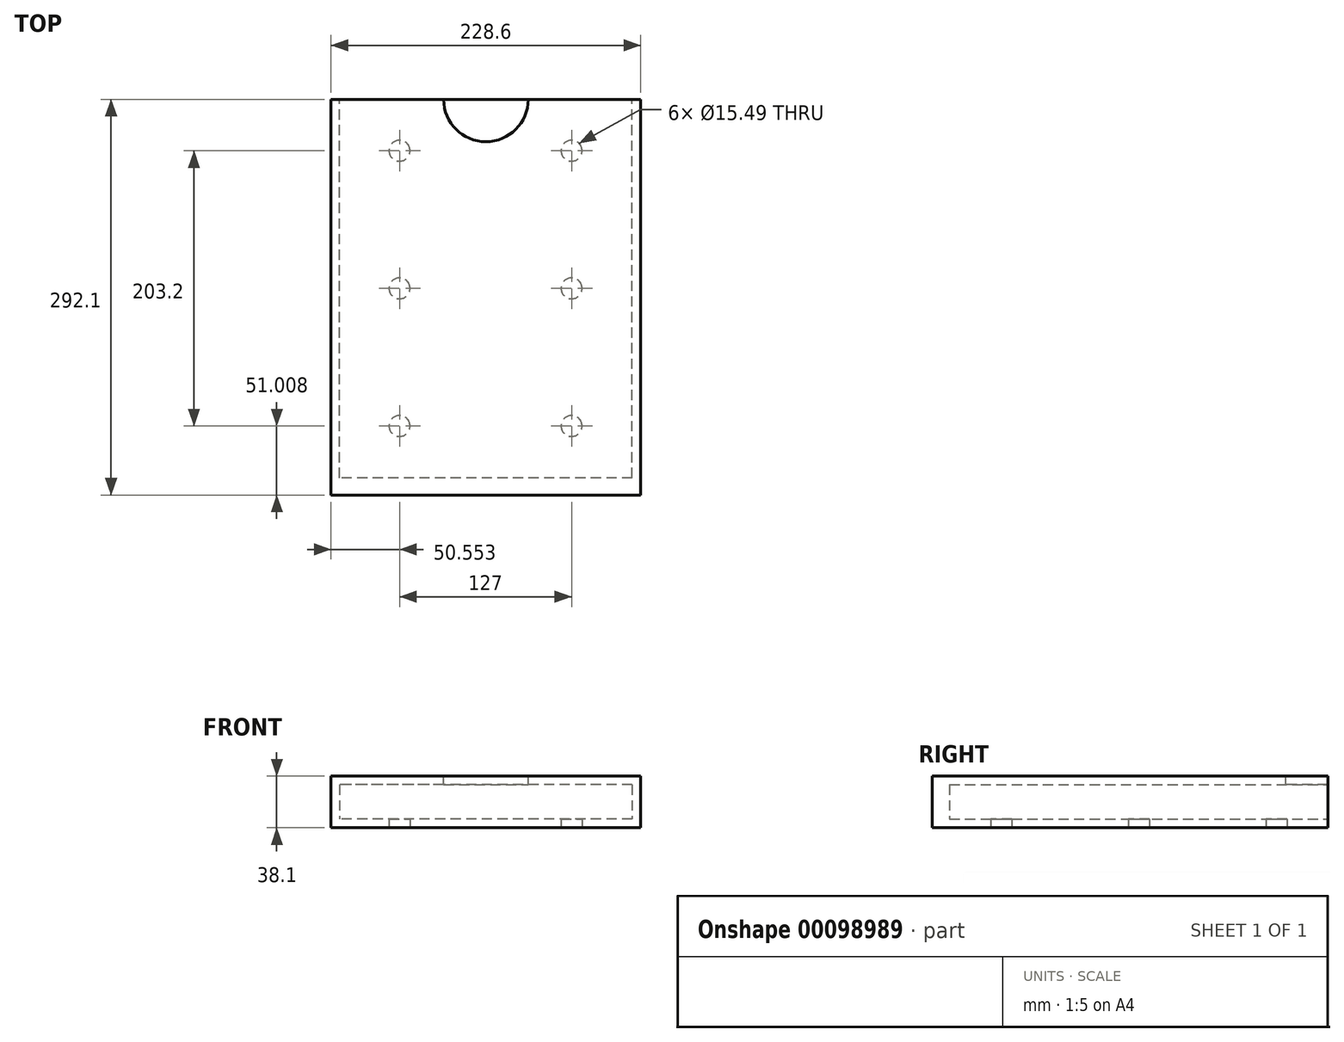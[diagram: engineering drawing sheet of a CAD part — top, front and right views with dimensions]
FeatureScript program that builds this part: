
annotation { "Feature Type Name" : "Feature", "Feature Type Description" : "" }
export const myFeature = defineFeature(function(context is Context, id is Id, definition is map)
    precondition{}
    {
        {
            var Q0;
            Q0=qCreatedBy(makeId("Top.planeOp"),FACE);
            var sketch = newSketch(context, id + "F0", { "sketchPlane" : qUnion([Q0])});
            skLineSegment(sketch, "E0.bottom", {"start": v(-114, 126.7) * mm, "end": v(114.6, 126.7) * mm});
            skLineSegment(sketch, "E0.top", {"start": v(-114, -165.4) * mm, "end": v(114.6, -165.4) * mm});
            skLineSegment(sketch, "E0.left", {"start": v(-114, 126.7) * mm, "end": v(-114, -165.4) * mm});
            skLineSegment(sketch, "E0.right", {"start": v(114.6, 126.7) * mm, "end": v(114.6, -165.4) * mm});
            skSolve(sketch);
        }
        {
            var Q0;
            Q0 = qSketchRegion(id + "F0", true);
            extrude(context, id + "F1", {"entities" : qUnion([Q0]), "depth" : 38.1 * mm});
        }
        {
            var Q0;
            Q0=makeQuery(id+"F1.opExtrude","SWEPT_FACE",FACE,{"disambiguationData":[OSD([sQuery(id+"F0.wireOp",EDGE,"E0.bottom")])]});
            var sketch = newSketch(context, id + "F2", { "sketchPlane" : qUnion([Q0])});
            skLineSegment(sketch, "E1.bottom", {"start": v(-108.25, 31.75) * mm, "end": v(107.65, 31.75) * mm});
            skLineSegment(sketch, "E1.top", {"start": v(-108.25, 6.35) * mm, "end": v(107.65, 6.35) * mm});
            skLineSegment(sketch, "E1.left", {"start": v(-108.25, 31.75) * mm, "end": v(-108.25, 6.35) * mm});
            skLineSegment(sketch, "E1.right", {"start": v(107.65, 31.75) * mm, "end": v(107.65, 6.35) * mm});
            skSolve(sketch);
        }
        {
            var Q0;
            Q0 = qSketchRegion(id + "F2", true);
            extrude(context, id + "F3", {"entities" : qUnion([Q0]), "operationType" : NewBodyOperationType.REMOVE, "oppositeDirection" : true, "depth" : 279.4 * mm});
        }
        {
            var Q0;
            Q0=makeQuery(id+"F1.opExtrude","CAP_FACE",FACE,{"disambiguationData":[OSD([sQuery(id+"F0.wireOp",EDGE,"E0.bottom"),sQuery(id+"F0.wireOp",EDGE,"E0.top"),sQuery(id+"F0.wireOp",EDGE,"E0.left"),sQuery(id+"F0.wireOp",EDGE,"E0.right")])],"isStart":false});
            var sketch = newSketch(context, id + "F4", { "sketchPlane" : qUnion([Q0])});
            skCircle(sketch, "E2", {"center": v(0.3, 126.7) * mm, "radius": 31.2 * mm});
            skSolve(sketch);
        }
        {
            var Q0;
            Q0 = qSketchRegion(id + "F4", true);
            extrude(context, id + "F5", {"entities" : qUnion([Q0]), "operationType" : NewBodyOperationType.REMOVE, "oppositeDirection" : true, "depth" : 6.35 * mm});
        }
        {
            var Q0;
            Q0=makeQuery(id+"F1.opExtrude","CAP_FACE",FACE,{"disambiguationData":[OSD([sQuery(id+"F0.wireOp",EDGE,"E0.bottom"),sQuery(id+"F0.wireOp",EDGE,"E0.top"),sQuery(id+"F0.wireOp",EDGE,"E0.left"),sQuery(id+"F0.wireOp",EDGE,"E0.right")])],"isStart":true});
            var sketch = newSketch(context, id + "F6", { "sketchPlane" : qUnion([Q0])});
            skCircle(sketch, "E3", {"center": v(-63.45, 114.4) * mm, "radius": 7.75 * mm});
            skCircle(sketch, "E4.0.1.0", {"center": v(-63.45, 12.8) * mm, "radius": 7.75 * mm});
            skCircle(sketch, "E4.0.2.0", {"center": v(-63.45, -88.8) * mm, "radius": 7.75 * mm});
            skCircle(sketch, "E4.1.0.0", {"center": v(63.55, 114.4) * mm, "radius": 7.75 * mm});
            skCircle(sketch, "E4.1.1.0", {"center": v(63.55, 12.8) * mm, "radius": 7.75 * mm});
            skCircle(sketch, "E4.1.2.0", {"center": v(63.55, -88.8) * mm, "radius": 7.75 * mm});
            skLineSegment(sketch, "E4.direction1", {"start": v(-63.45, 114.4) * mm, "end": v(63.55, 114.4) * mm, "construction": true});
            skLineSegment(sketch, "E4.direction2", {"start": v(-63.45, 114.4) * mm, "end": v(-63.45, 12.8) * mm, "construction": true});
            skSolve(sketch);
        }
        {
            var Q0;
            Q0 = qSketchRegion(id + "F6", true);
            extrude(context, id + "F7", {"entities" : qUnion([Q0]), "operationType" : NewBodyOperationType.REMOVE, "oppositeDirection" : true, "depth" : 6.35 * mm});
        }
    });
